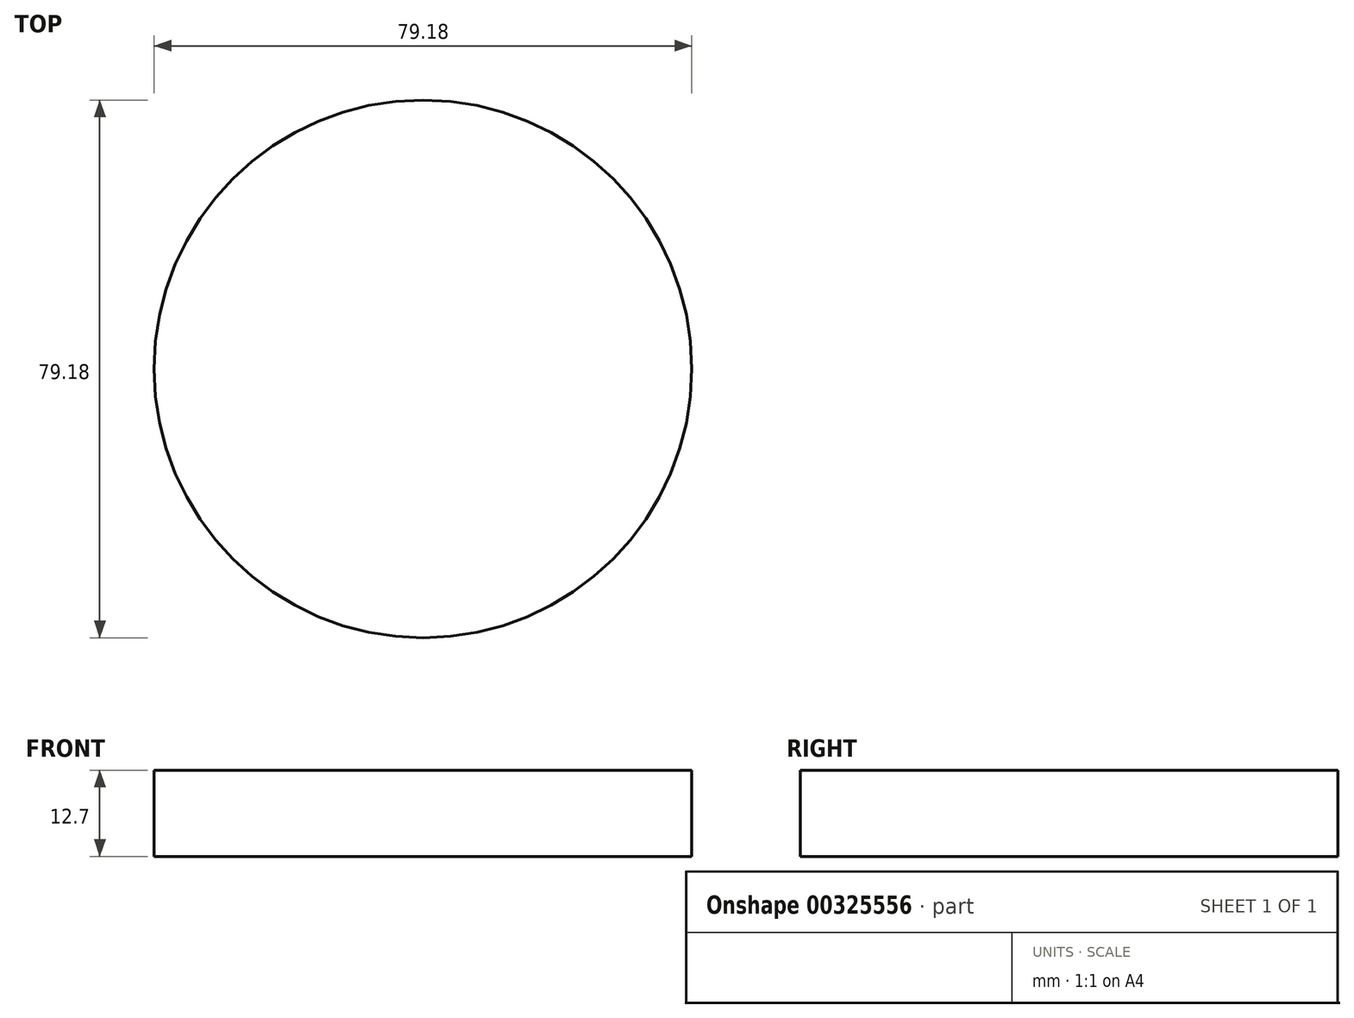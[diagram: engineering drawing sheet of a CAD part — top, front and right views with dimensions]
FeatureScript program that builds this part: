
annotation { "Feature Type Name" : "Feature", "Feature Type Description" : "" }
export const myFeature = defineFeature(function(context is Context, id is Id, definition is map)
    precondition{}
    {
        {
            var Q0;
            Q0=qCreatedBy(makeId("Front.planeOp"),FACE);
            var sketch = newSketch(context, id + "F0", { "sketchPlane" : qUnion([Q0])});
            skLineSegment(sketch, "E0.bottom", {"start": v(0, 0) * mm, "end": v(39.6, 0) * mm});
            skLineSegment(sketch, "E0.top", {"start": v(0, 12.7) * mm, "end": v(39.6, 12.7) * mm});
            skLineSegment(sketch, "E0.left", {"start": v(0, 0) * mm, "end": v(0, 12.7) * mm});
            skLineSegment(sketch, "E0.right", {"start": v(39.6, 0) * mm, "end": v(39.6, 12.7) * mm});
            skLineSegment(sketch, "E1.bottom", {"start": v(39.6, 0) * mm, "end": v(52.3, 0) * mm});
            skLineSegment(sketch, "E1.top", {"start": v(39.6, 12.7) * mm, "end": v(52.3, 12.7) * mm});
            skLineSegment(sketch, "E1.right", {"start": v(52.3, 0) * mm, "end": v(52.3, 12.7) * mm});
            skSolve(sketch);
        }
        {
            var Q0;
            Q0=makeQuery(id+"F0.imprint","IMPRINT",FACE,{"disambiguationData":[TD([[makeQuery(id+"F0.imprint","IMPRINT",EDGE,{"derivedFrom":sQuery(id+"F0.wireOp",EDGE,"E0.bottom")}),1.0]])]});
            var Q1;
            Q1=sQuery(id+"F0.wireOp",EDGE,"E0.left");
            revolve(context, id + "F1", {"entities" : qUnion([Q0]), "axis" : qUnion([Q1]), "revolveType" : RevolveType.FULL});
        }
    });
